# Revit family: QF_MOFFAT WALDORF_FNL8127EE
name_source: partatom
category: Specialty Equipment
revit_build: Autodesk Revit Architecture 2012 (Build: 20110916_2132(x64)
units: mm (PartAtom-declared; Revit-internal decimal feet)

## types (1)
- QF_MOFFAT WALDORF_FNL8127EE
    Apparent Power = 16944 VA
    Body Finish = QF_Finishes_Stainless Steel
    Conn Conduit = Yes
    Cycle = 50 Hz
    Description = FRYER LOW SPLASHBACK WITH CONTROLLER SINGLE PAN ELECTRIC
    FL Amps = 24 A
    Height = 1085 mm  [stored 3.55971 ft]
    Manufacturer = MOFFAT WALDORF
    Max Overcurrent Protection = 0 A
    Min Ckt Ampacity = 0 A
    Model = FNL8127EE
    Phase = 3
    URL = www.moffat.com
    URL Cutsheet = www.moffat.com
    Volts = 415 V
    Watts = 17000 W
    Weight in Pounds = 141.0957

note: [stored X ft] marks values corroborated as IEEE doubles in the binary element streams (Revit-internal decimal feet)

## geometry (parser evidence)
native form markers: Blend x15, Sweep x2
no freeform markers — native parametric forms only
